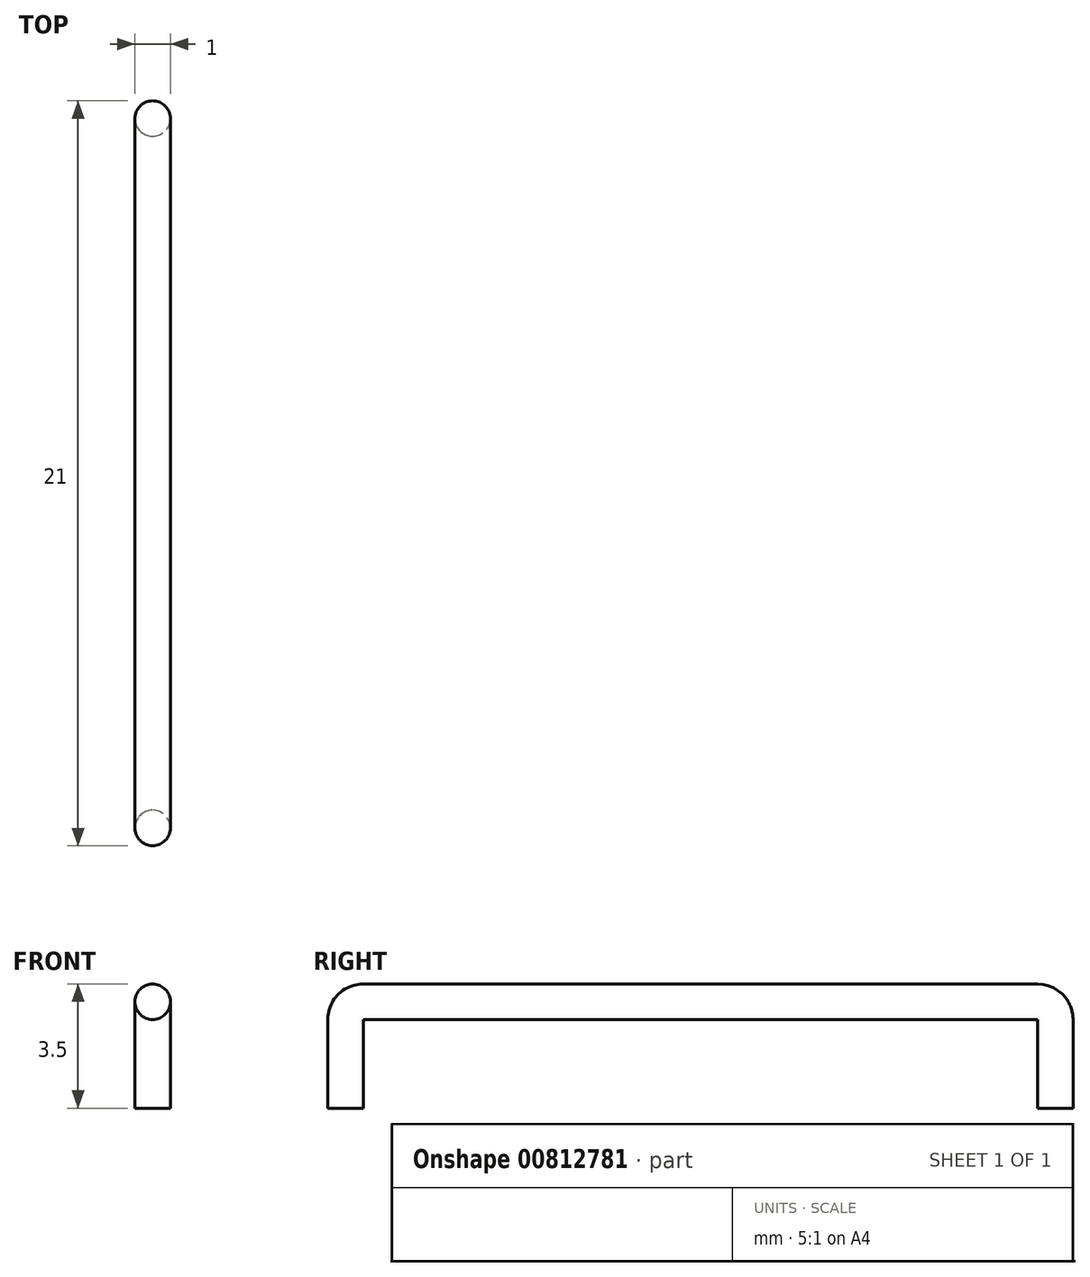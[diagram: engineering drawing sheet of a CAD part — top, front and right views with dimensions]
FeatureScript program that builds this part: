
annotation { "Feature Type Name" : "Feature", "Feature Type Description" : "" }
export const myFeature = defineFeature(function(context is Context, id is Id, definition is map)
    precondition{}
    {
        {
            var Q0;
            Q0=qCreatedBy(makeId("Right.planeOp"),FACE);
            var sketch = newSketch(context, id + "F0", { "sketchPlane" : qUnion([Q0])});
            skLineSegment(sketch, "E0", {"start": v(-10, 0) * mm, "end": v(-10, 2.5) * mm});
            skLineSegment(sketch, "E1", {"start": v(-9.5, 3) * mm, "end": v(9.5, 3) * mm});
            skLineSegment(sketch, "E2", {"start": v(10, 2.5) * mm, "end": v(10, 0) * mm});
            skPoint(sketch, "E3.visualSharp", {"position": v(-10, 3) * mm});
            skArc(sketch, "E3.filletArc", {"start": v(-9.5, 3) * mm, "mid": v(-9.85, 2.85) * mm, "end": v(-10, 2.5) * mm});
            skPoint(sketch, "E4.visualSharp", {"position": v(10, 3) * mm});
            skArc(sketch, "E4.filletArc", {"start": v(10, 2.5) * mm, "mid": v(9.85, 2.85) * mm, "end": v(9.5, 3) * mm});
            skSolve(sketch);
        }
        {
            var Q0;
            Q0=qCreatedBy(makeId("Top.planeOp"),FACE);
            var sketch = newSketch(context, id + "F1", { "sketchPlane" : qUnion([Q0])});
            skCircle(sketch, "E5", {"center": v(0, -10) * mm, "radius": 0.5 * mm});
            skSolve(sketch);
        }
        {
            var Q0;
            Q0=makeQuery(id+"F1.imprint","IMPRINT",FACE,{"disambiguationData":[TD([[makeQuery(id+"F1.imprint","IMPRINT",EDGE,{"derivedFrom":sQuery(id+"F1.wireOp",EDGE,"E5")}),1.0]])]});
            var Q1;
            Q1=sQuery(id+"F0.wireOp",EDGE,"E0");
            var Q2;
            Q2=sQuery(id+"F0.wireOp",EDGE,"E3.filletArc");
            var Q3;
            Q3=sQuery(id+"F0.wireOp",EDGE,"E1");
            var Q4;
            Q4=sQuery(id+"F0.wireOp",EDGE,"E4.filletArc");
            var Q5;
            Q5=sQuery(id+"F0.wireOp",EDGE,"E2");
            sweep(context, id + "F2", {"profiles" : qUnion([Q0]), "path" : qUnion([Q1, Q2, Q3, Q4, Q5])});
        }
    });
